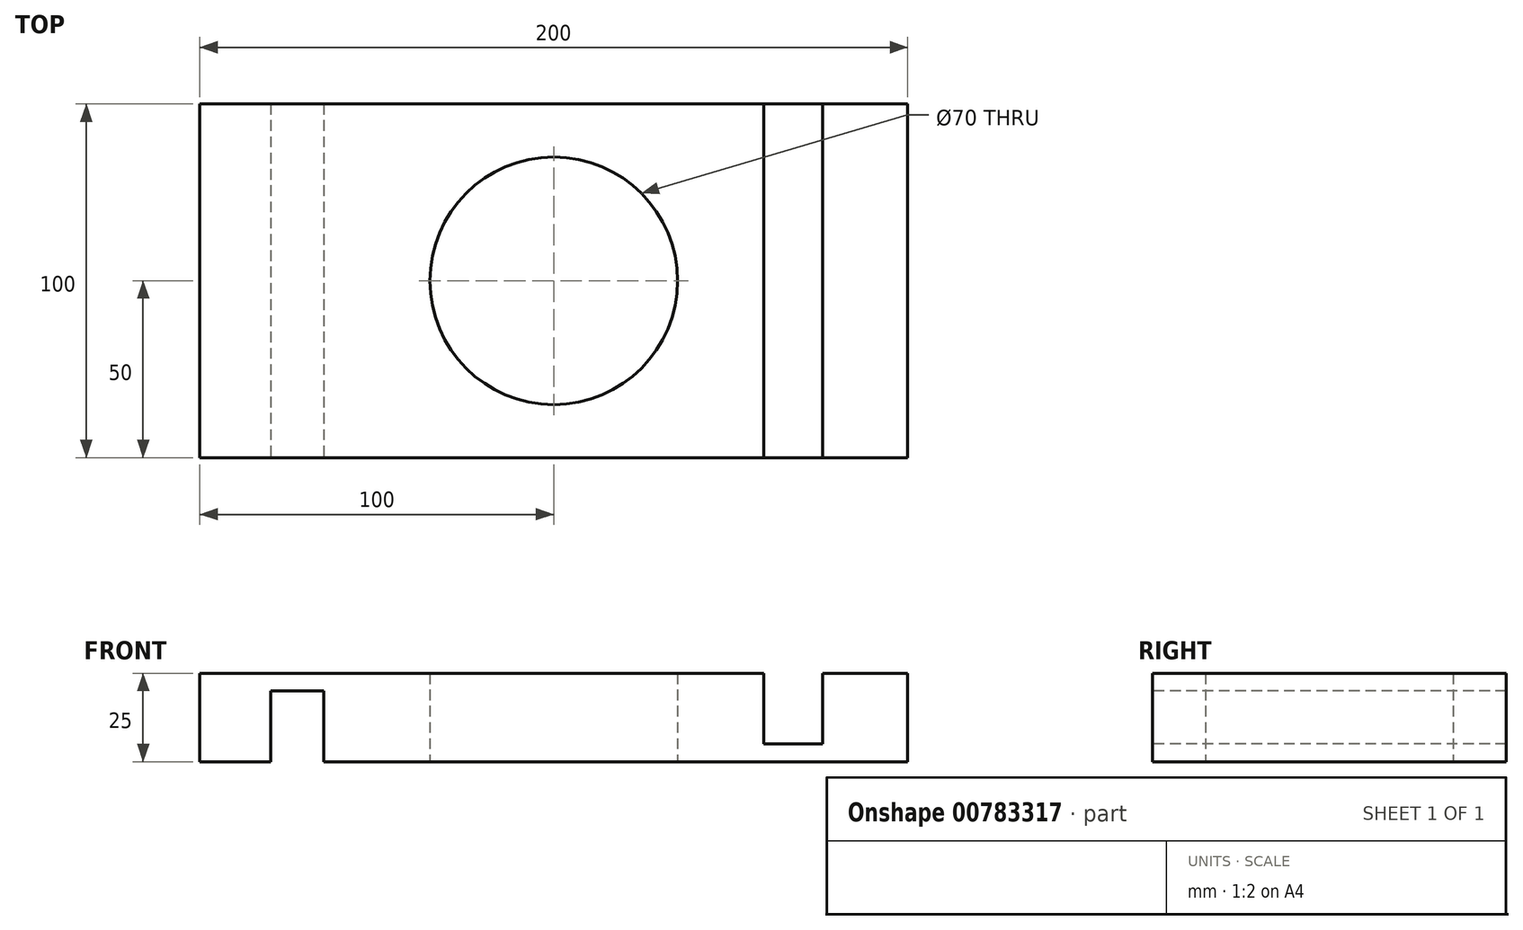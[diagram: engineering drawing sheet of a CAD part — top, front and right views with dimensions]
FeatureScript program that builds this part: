
annotation { "Feature Type Name" : "Feature", "Feature Type Description" : "" }
export const myFeature = defineFeature(function(context is Context, id is Id, definition is map)
    precondition{}
    {
        {
            var Q0;
            Q0=qCreatedBy(makeId("Top.planeOp"),FACE);
            var sketch = newSketch(context, id + "F0", { "sketchPlane" : qUnion([Q0])});
            skLineSegment(sketch, "E0.bottom", {"start": v(-100, 50) * mm, "end": v(100, 50) * mm});
            skLineSegment(sketch, "E0.top", {"start": v(-100, -50) * mm, "end": v(100, -50) * mm});
            skLineSegment(sketch, "E0.left", {"start": v(-100, 50) * mm, "end": v(-100, -50) * mm});
            skLineSegment(sketch, "E0.right", {"start": v(100, 50) * mm, "end": v(100, -50) * mm});
            skPoint(sketch, "E0.middle", {"position": v(0, 0) * mm});
            skCircle(sketch, "E1", {"center": v(0, 0) * mm, "radius": 35 * mm});
            skSolve(sketch);
        }
        {
            var Q0;
            Q0=makeQuery(id+"F0.imprint","IMPRINT",FACE,{"disambiguationData":[TD([[makeQuery(id+"F0.imprint","IMPRINT",EDGE,{"derivedFrom":sQuery(id+"F0.wireOp",EDGE,"E0.bottom")}),-1.0]])]});
            extrude(context, id + "F1", {"entities" : qUnion([Q0]), "depth" : 25 * mm, "offsetDistance" : 25 * mm});
        }
        {
            var Q0;
            Q0=qCreatedBy(makeId("Top.planeOp"),FACE);
            var sketch = newSketch(context, id + "F2", { "sketchPlane" : qUnion([Q0])});
            skLineSegment(sketch, "E2.bottom", {"start": v(-80, 51.7) * mm, "end": v(-65, 51.7) * mm});
            skLineSegment(sketch, "E2.top", {"start": v(-80, -51.53) * mm, "end": v(-65, -51.53) * mm});
            skLineSegment(sketch, "E2.left", {"start": v(-80, 51.7) * mm, "end": v(-80, -51.53) * mm});
            skLineSegment(sketch, "E2.right", {"start": v(-65, 51.7) * mm, "end": v(-65, -51.53) * mm});
            skSolve(sketch);
        }
        {
            var Q0;
            Q0=makeQuery(id+"F1.opExtrude","CAP_FACE",FACE,{"disambiguationData":[OSD([sQuery(id+"F0.wireOp",EDGE,"E0.bottom"),sQuery(id+"F0.wireOp",EDGE,"E0.top"),sQuery(id+"F0.wireOp",EDGE,"E0.left"),sQuery(id+"F0.wireOp",EDGE,"E0.right"),sQuery(id+"F0.wireOp",EDGE,"E1")])],"isStart":false});
            var sketch = newSketch(context, id + "F3", { "sketchPlane" : qUnion([Q0])});
            skLineSegment(sketch, "E3.bottom", {"start": v(75.99, 50) * mm, "end": v(59.4, 50) * mm});
            skLineSegment(sketch, "E3.top", {"start": v(75.99, -50) * mm, "end": v(59.4, -50) * mm});
            skLineSegment(sketch, "E3.left", {"start": v(75.99, 50) * mm, "end": v(75.99, -50) * mm});
            skLineSegment(sketch, "E3.right", {"start": v(59.4, 50) * mm, "end": v(59.4, -50) * mm});
            skSolve(sketch);
        }
        {
            var Q0;
            Q0=makeQuery(id+"F3.imprint","IMPRINT",FACE,{"disambiguationData":[TD([[makeQuery(id+"F3.imprint","IMPRINT",EDGE,{"derivedFrom":sQuery(id+"F3.wireOp",EDGE,"E3.bottom")}),-1.0]])]});
            extrude(context, id + "F4", {"entities" : qUnion([Q0]), "operationType" : NewBodyOperationType.REMOVE, "oppositeDirection" : true, "depth" : 20 * mm, "offsetDistance" : 25 * mm});
        }
        {
            var Q0;
            Q0=makeQuery(id+"F2.imprint","IMPRINT",FACE,{"disambiguationData":[TD([[makeQuery(id+"F2.imprint","IMPRINT",EDGE,{"derivedFrom":sQuery(id+"F2.wireOp",EDGE,"E2.bottom")}),-1.0]])]});
            extrude(context, id + "F5", {"entities" : qUnion([Q0]), "operationType" : NewBodyOperationType.REMOVE, "depth" : 20 * mm, "offsetDistance" : 25 * mm});
        }
    });
